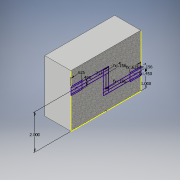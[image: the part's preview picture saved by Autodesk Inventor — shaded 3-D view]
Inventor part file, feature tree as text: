
AUTODESK INVENTOR PART (.ipt)
format: ipt  version: 2018 (Build 220112000, 112)  size: 124,416 bytes
history: native  units: in
note: dims shown in document units (in); Inventor stores cm internally (conversion verified against a paired STEP export)
features: sketch x2, extrude x1
ambient origin geometry x8: Origin, YZ Plane, XZ Plane, XY Plane, X Axis, Y Axis, Z Axis, Center Point
bodies: Solid1 (feature_tree)
feature tree (3):
  extrude  "Extrusion1"  Depth=4.0in
  sketch  "Sketch2"  dims[d2=3.0in d3=0.0in d4=0.3125in d7=0.1562in d8=0.1562in d9=0.1562in d10=0.45in d11=0.45in d12=0.625in d13=0.625in d42=2.0in d43=1.0in]
  sketch  "Sketch1"  dims[d0=3.0in d1=4.0in]
